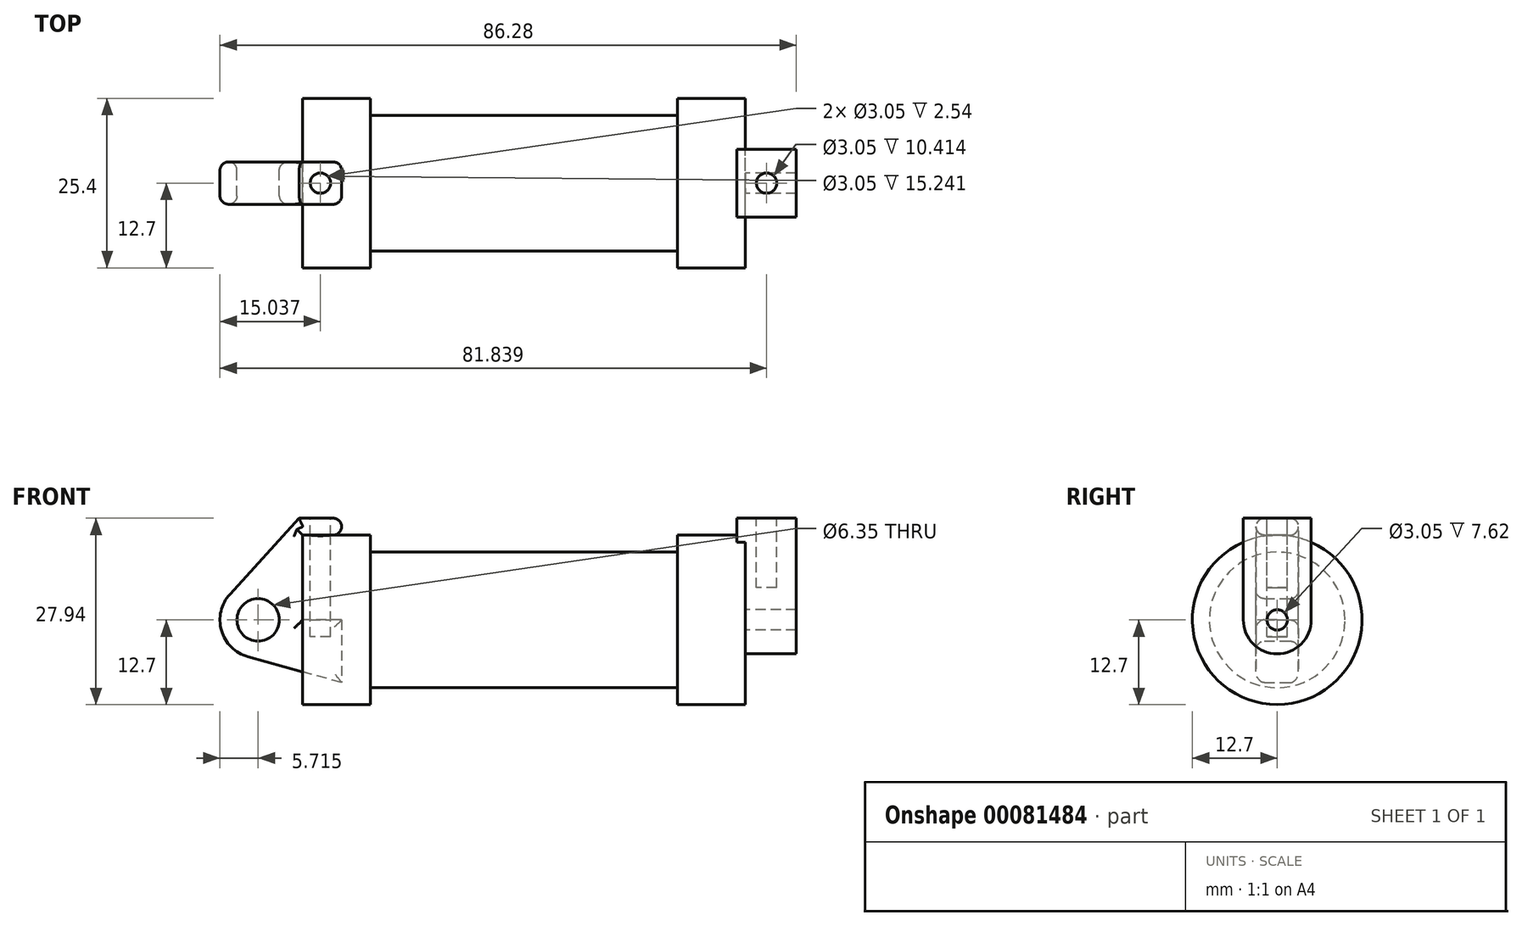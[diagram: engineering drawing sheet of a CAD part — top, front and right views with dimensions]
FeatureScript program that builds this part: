
annotation { "Feature Type Name" : "Feature", "Feature Type Description" : "" }
export const myFeature = defineFeature(function(context is Context, id is Id, definition is map)
    precondition{}
    {
        {
            var Q0;
            Q0=qCreatedBy(makeId("Front.planeOp"),FACE);
            var sketch = newSketch(context, id + "F0", { "sketchPlane" : qUnion([Q0])});
            skLineSegment(sketch, "E0", {"start": v(0, 0) * mm, "end": v(0, 12.7) * mm});
            skLineSegment(sketch, "E1", {"start": v(0, 12.7) * mm, "end": v(10.16, 12.7) * mm});
            skLineSegment(sketch, "E2", {"start": v(10.16, 12.7) * mm, "end": v(10.16, 10.16) * mm});
            skLineSegment(sketch, "E3", {"start": v(10.16, 10.16) * mm, "end": v(56.13, 10.16) * mm});
            skLineSegment(sketch, "E4", {"start": v(56.13, 10.16) * mm, "end": v(56.13, 12.7) * mm});
            skLineSegment(sketch, "E5", {"start": v(56.13, 12.7) * mm, "end": v(66.3, 12.7) * mm});
            skLineSegment(sketch, "E6", {"start": v(66.3, 12.7) * mm, "end": v(66.3, 0) * mm});
            skLineSegment(sketch, "E7", {"start": v(66.3, 0) * mm, "end": v(0, 0) * mm});
            skLineSegment(sketch, "E8", {"start": v(5.84, 15.24) * mm, "end": v(-0.5, 15.24) * mm});
            skLineSegment(sketch, "E9", {"start": v(-0.5, 15.24) * mm, "end": v(-10.88, 3.85) * mm});
            skLineSegment(sketch, "E10", {"start": v(0, 0) * mm, "end": v(-6.65, 0) * mm});
            skCircle(sketch, "E11", {"center": v(-6.65, 0) * mm, "radius": 5.72 * mm});
            skCircle(sketch, "E12", {"center": v(-6.65, 0) * mm, "radius": 3.18 * mm});
            skLineSegment(sketch, "E13", {"start": v(5.84, 15.24) * mm, "end": v(5.84, -9.4) * mm});
            skLineSegment(sketch, "E14", {"start": v(5.84, -9.4) * mm, "end": v(-8.18, -5.5) * mm});
            skSolve(sketch);
        }
        {
            var Q0;
            {var subQ0=sQuery(id+"F0.wireOp",EDGE,"E2");Q0=makeQuery(id+"F0.imprint","IMPRINT",FACE,{"disambiguationData":[TD([[makeQuery(id+"F0.imprint","IMPRINT",EDGE,{"derivedFrom":subQ0}),-1.0]])]});}
            var Q1;
            {var subQ0=sQuery(id+"F0.wireOp",EDGE,"E0");Q1=makeQuery(id+"F0.imprint","IMPRINT",FACE,{"disambiguationData":[TD([[makeQuery(id+"F0.imprint","IMPRINT",EDGE,{"derivedFrom":subQ0}),-1.0]])]});}
            var Q2;
            Q2=sQuery(id+"F0.wireOp",EDGE,"E7");
            revolve(context, id + "F1", {"entities" : qUnion([Q0, Q1]), "axis" : qUnion([Q2]), "revolveType" : RevolveType.FULL});
        }
        {
            var Q0;
            {var subQ3=sQuery(id+"F0.wireOp",EDGE,"E0");Q0=makeQuery(id+"F0.imprint","IMPRINT",FACE,{"disambiguationData":[TD([[makeQuery(id+"F0.imprint","IMPRINT",EDGE,{"derivedFrom":subQ3}),1.0]])]});}
            var Q1;
            {var subQ4=sQuery(id+"F0.wireOp",EDGE,"E12");Q1=makeQuery(id+"F0.imprint","IMPRINT",FACE,{"disambiguationData":[TD([[makeQuery(id+"F0.imprint","IMPRINT",EDGE,{"derivedFrom":subQ4}),-1.0]])]});}
            var Q2;
            {var subQ0=sQuery(id+"F0.wireOp",EDGE,"E14");Q2=makeQuery(id+"F0.imprint","IMPRINT",FACE,{"disambiguationData":[TD([[makeQuery(id+"F0.imprint","IMPRINT",EDGE,{"derivedFrom":subQ0}),-1.0]])]});}
            extrude(context, id + "F2", {"entities" : qUnion([Q0, Q1, Q2]), "endBound" : BoundingType.SYMMETRIC, "depth" : 6.35 * mm});
        }
        {
            var Q0;
            Q0=makeQuery(id+"F1.opRevolve","SWEPT_FACE",FACE,{"disambiguationData":[OSD([sQuery(id+"F0.wireOp",EDGE,"E6")])]});
            var sketch = newSketch(context, id + "F3", { "sketchPlane" : qUnion([Q0])});
            skCircle(sketch, "E15", {"center": v(0, 0) * mm, "radius": 1.52 * mm});
            skCircle(sketch, "E16", {"center": v(0, 0) * mm, "radius": 5.08 * mm});
            skLineSegment(sketch, "E17", {"start": v(5.08, 0) * mm, "end": v(5.08, 15.24) * mm});
            skLineSegment(sketch, "E18", {"start": v(-5.08, 0) * mm, "end": v(-5.08, 15.24) * mm});
            skLineSegment(sketch, "E19", {"start": v(-5.08, 15.24) * mm, "end": v(5.08, 15.24) * mm});
            skSolve(sketch);
        }
        {
            var Q0;
            Q0=makeQuery(id+"F3.imprint","IMPRINT",FACE,{"disambiguationData":[TD([[makeQuery(id+"F3.imprint","IMPRINT",EDGE,{"derivedFrom":sQuery(id+"F3.wireOp",EDGE,"E15")}),-1.0]])]});
            var Q1;
            {var subQ0=sQuery(id+"F3.wireOp",EDGE,"E19");Q1=makeQuery(id+"F3.imprint","IMPRINT",FACE,{"disambiguationData":[TD([[makeQuery(id+"F3.imprint","IMPRINT",EDGE,{"derivedFrom":subQ0}),-1.0]])]});}
            var Q2;
            {var subQ0=sQuery(id+"F3.wireOp",EDGE,"E17");var subQ1=sQuery(id+"F3.wireOp",EDGE,"E16");var subQ2=makeQuery(id+"F3.imprint","INTERSECT",VERTEX,{"derivedFrom":[subQ1,subQ0]});Q2=makeQuery(id+"F3.imprint","IMPRINT",FACE,{"disambiguationData":[TD([[makeQuery(id+"F3.imprint","IMPRINT",EDGE,{"disambiguationData":[TD([[subQ2,-1.0]])],"derivedFrom":subQ1}),-1.0]])]});}
            extrude(context, id + "F4", {"entities" : qUnion([Q0, Q1, Q2]), "operationType" : NewBodyOperationType.ADD, "depth" : 7.62 * mm});
        }
        {
            var Q0;
            Q0=makeQuery(id+"F4.opExtrude","CAP_FACE",FACE,{"disambiguationData":[OSD([sQuery(id+"F3.wireOp",EDGE,"E15"),sQuery(id+"F3.wireOp",EDGE,"E16"),sQuery(id+"F3.wireOp",EDGE,"E17"),sQuery(id+"F3.wireOp",EDGE,"E18"),sQuery(id+"F3.wireOp",EDGE,"E19")])],"isStart":true});
            extrude(context, id + "F5", {"entities" : qUnion([Q0]), "operationType" : NewBodyOperationType.ADD, "depth" : 1.27 * mm});
        }
        {
            var Q0;
            Q0=makeQuery(id+"F4.boolean.opBoolean","SPLIT",FACE,{"disambiguationData":[TD([makeQuery(id+"F4.opExtrude","SWEPT_FACE",FACE,{"disambiguationData":[OSD([sQuery(id+"F3.wireOp",EDGE,"E15")])]})])],"derivedFrom":makeQuery(id+"F1.opRevolve","SWEPT_FACE",FACE,{"disambiguationData":[OSD([sQuery(id+"F0.wireOp",EDGE,"E6")])]})});
            extrude(context, id + "F6", {"entities" : qUnion([Q0]), "operationType" : NewBodyOperationType.ADD, "oppositeDirection" : true, "depth" : 1.27 * mm});
        }
        {
            var Q0;
            {var subQ0=sQuery(id+"F3.wireOp",EDGE,"E19");Q0=makeQuery(id+"F5.boolean.opBoolean","MERGE",FACE,{"derivedFrom":[makeQuery(id+"F4.opExtrude","SWEPT_FACE",FACE,{"disambiguationData":[OSD([subQ0])]}),makeQuery(id+"F5.opExtrude","SWEPT_FACE",FACE,{"disambiguationData":[OSD([subQ0])]})]});}
            var sketch = newSketch(context, id + "F7", { "sketchPlane" : qUnion([Q0])});
            skCircle(sketch, "E20", {"center": v(69.47, 0) * mm, "radius": 1.52 * mm});
            skSolve(sketch);
        }
        {
            var Q0;
            Q0=makeQuery(id+"F7.imprint","IMPRINT",FACE,{"disambiguationData":[TD([[makeQuery(id+"F7.imprint","IMPRINT",EDGE,{"derivedFrom":sQuery(id+"F7.wireOp",EDGE,"E20")}),1.0]])]});
            extrude(context, id + "F8", {"entities" : qUnion([Q0]), "operationType" : NewBodyOperationType.REMOVE, "oppositeDirection" : true, "depth" : 10.4 * mm});
        }
        {
            var Q0;
            Q0=makeQuery(id+"F1.opRevolve","SWEPT_EDGE",EDGE,{"disambiguationData":[OSD([sQuery(id+"F0.wireOp",EDGE,"E0"),sQuery(id+"F0.wireOp",EDGE,"E1")])]});
            var Q1;
            Q1=makeQuery(id+"F1.opRevolve","SWEPT_EDGE",EDGE,{"disambiguationData":[OSD([sQuery(id+"F0.wireOp",EDGE,"E1"),sQuery(id+"F0.wireOp",EDGE,"E2")])]});
            var Q2;
            Q2=makeQuery(id+"F1.opRevolve","SWEPT_EDGE",EDGE,{"disambiguationData":[OSD([sQuery(id+"F0.wireOp",EDGE,"E4"),sQuery(id+"F0.wireOp",EDGE,"E5")])]});
            var Q3;
            Q3=makeQuery(id+"F4.boolean.opBoolean","SPLIT",EDGE,{"disambiguationData":[OD(1.0)],"derivedFrom":makeQuery(id+"F1.opRevolve","SWEPT_EDGE",EDGE,{"disambiguationData":[OSD([sQuery(id+"F0.wireOp",EDGE,"E5"),sQuery(id+"F0.wireOp",EDGE,"E6")])]})});
            var Q4;
            Q4=makeQuery(id+"F4.opExtrude","CAP_EDGE",EDGE,{"disambiguationData":[OSD([sQuery(id+"F3.wireOp",EDGE,"E18")])],"isStart":false});
            var Q5;
            Q5=makeQuery(id+"F4.opExtrude","SWEPT_EDGE",EDGE,{"disambiguationData":[OSD([sQuery(id+"F3.wireOp",EDGE,"E16"),sQuery(id+"F3.wireOp",EDGE,"E18")])]});
            var Q6;
            {var subQ0=sQuery(id+"F3.wireOp",EDGE,"E16");var subQ1=sQuery(id+"F3.wireOp",EDGE,"E18");Q6=makeQuery(id+"F4.boolean.opBoolean","SPLIT",EDGE,{"disambiguationData":[TD([makeQuery(id+"F4.opExtrude","SWEPT_FACE",FACE,{"disambiguationData":[OSD([subQ0])]})])],"derivedFrom":makeQuery(id+"F4.opExtrude","CAP_EDGE",EDGE,{"disambiguationData":[OSD([subQ1])],"isStart":true})});}
            var Q7;
            Q7=makeQuery(id+"F5.opExtrude","CAP_EDGE",EDGE,{"disambiguationData":[OSD([sQuery(id+"F3.wireOp",EDGE,"E18")])],"isStart":false});
            var Q8;
            Q8=makeQuery(id+"F5.opExtrude","CAP_EDGE",EDGE,{"disambiguationData":[OSD([sQuery(id+"F3.wireOp",EDGE,"E19")])],"isStart":false});
            var Q9;
            {var subQ0=sQuery(id+"F3.wireOp",EDGE,"E19");var subQ1=sQuery(id+"F3.wireOp",EDGE,"E18");Q9=makeQuery(id+"F5.boolean.opBoolean","MERGE",EDGE,{"derivedFrom":[makeQuery(id+"F4.opExtrude","SWEPT_EDGE",EDGE,{"disambiguationData":[OSD([subQ1,subQ0])]}),makeQuery(id+"F5.opExtrude","SWEPT_EDGE",EDGE,{"disambiguationData":[OSD([subQ1,subQ0])]})]});}
            var Q10;
            Q10=makeQuery(id+"F4.opExtrude","CAP_EDGE",EDGE,{"disambiguationData":[OSD([sQuery(id+"F3.wireOp",EDGE,"E19")])],"isStart":false});
            var Q11;
            {var subQ0=sQuery(id+"F3.wireOp",EDGE,"E19");var subQ1=sQuery(id+"F3.wireOp",EDGE,"E17");Q11=makeQuery(id+"F5.boolean.opBoolean","MERGE",EDGE,{"derivedFrom":[makeQuery(id+"F4.opExtrude","SWEPT_EDGE",EDGE,{"disambiguationData":[OSD([subQ1,subQ0])]}),makeQuery(id+"F5.opExtrude","SWEPT_EDGE",EDGE,{"disambiguationData":[OSD([subQ1,subQ0])]})]});}
            var Q12;
            Q12=makeQuery(id+"F4.opExtrude","CAP_EDGE",EDGE,{"disambiguationData":[OSD([sQuery(id+"F3.wireOp",EDGE,"E16")])],"isStart":false});
            var Q13;
            Q13=makeQuery(id+"F4.opExtrude","CAP_EDGE",EDGE,{"disambiguationData":[OSD([sQuery(id+"F3.wireOp",EDGE,"E16")])],"isStart":true});
            var Q14;
            Q14=makeQuery(id+"F4.opExtrude","CAP_EDGE",EDGE,{"disambiguationData":[OSD([sQuery(id+"F3.wireOp",EDGE,"E17")])],"isStart":false});
            var Q15;
            {var subQ0=sQuery(id+"F3.wireOp",EDGE,"E16");var subQ1=sQuery(id+"F3.wireOp",EDGE,"E17");Q15=makeQuery(id+"F4.boolean.opBoolean","SPLIT",EDGE,{"disambiguationData":[TD([makeQuery(id+"F4.opExtrude","SWEPT_FACE",FACE,{"disambiguationData":[OSD([subQ0])]})])],"derivedFrom":makeQuery(id+"F4.opExtrude","CAP_EDGE",EDGE,{"disambiguationData":[OSD([subQ1])],"isStart":true})});}
            var Q16;
            Q16=makeQuery(id+"F5.opExtrude","CAP_EDGE",EDGE,{"disambiguationData":[OSD([sQuery(id+"F3.wireOp",EDGE,"E17")])],"isStart":false});
            var Q17;
            Q17=makeQuery(id+"F1.opRevolve","SWEPT_EDGE",EDGE,{"disambiguationData":[OSD([sQuery(id+"F0.wireOp",EDGE,"E2"),sQuery(id+"F0.wireOp",EDGE,"E3")])]});
            var Q18;
            Q18=makeQuery(id+"F1.opRevolve","SWEPT_EDGE",EDGE,{"disambiguationData":[OSD([sQuery(id+"F0.wireOp",EDGE,"E3"),sQuery(id+"F0.wireOp",EDGE,"E4")])]});
            var Q19;
            {var subQ0=sQuery(id+"F3.wireOp",EDGE,"E17");var subQ1=sQuery(id+"F3.wireOp",EDGE,"E19");var subQ2=sQuery(id+"F3.wireOp",EDGE,"E18");var subQ3=sQuery(id+"F3.wireOp",EDGE,"E16");var subQ4=sQuery(id+"F3.wireOp",EDGE,"E15");var subQ5=sQuery(id+"F0.wireOp",EDGE,"E6");var subQ6=sQuery(id+"F0.wireOp",EDGE,"E5");Q19=makeQuery(id+"F5.opExtrude","SWEPT_EDGE",EDGE,{"disambiguationData":[OSD([subQ6,subQ5,subQ4,subQ3,subQ0,subQ2,subQ1]),TDD([makeQuery(id+"F4.boolean.opBoolean","TWEAK_VERTEX",VERTEX,{"derivedFrom":[makeQuery(id+"F1.opRevolve","SWEPT_FACE",FACE,{"disambiguationData":[OSD([subQ6])]}),makeQuery(id+"F1.opRevolve","SWEPT_FACE",FACE,{"disambiguationData":[OSD([subQ5])]}),makeQuery(id+"F4.opExtrude","CAP_FACE",FACE,{"disambiguationData":[OSD([subQ4,subQ3,subQ0,subQ2,subQ1])],"isStart":true}),makeQuery(id+"F4.opExtrude","SWEPT_FACE",FACE,{"disambiguationData":[OSD([subQ0])]})]})])]});}
            var Q20;
            {var subQ0=sQuery(id+"F0.wireOp",EDGE,"E13");Q20=makeQuery(id+"F2.opExtrude","CAP_EDGE",EDGE,{"disambiguationData":[OSD([subQ0]),TDD([makeQuery(id+"F0.imprint","IMPRINT",EDGE,{"disambiguationData":[TD([[makeQuery(id+"F0.imprint","INTERSECT",VERTEX,{"derivedFrom":[sQuery(id+"F0.wireOp",EDGE,"E8"),subQ0]}),-1.0]])],"derivedFrom":subQ0})])],"isStart":false});}
            var Q21;
            Q21=makeQuery(id+"F2.opExtrude","SWEPT_EDGE",EDGE,{"disambiguationData":[OSD([sQuery(id+"F0.wireOp",EDGE,"E8"),sQuery(id+"F0.wireOp",EDGE,"E13")])]});
            var Q22;
            Q22=makeQuery(id+"F2.opExtrude","SWEPT_EDGE",EDGE,{"disambiguationData":[OSD([sQuery(id+"F0.wireOp",EDGE,"E1"),sQuery(id+"F0.wireOp",EDGE,"E13")])]});
            var Q23;
            {var subQ0=sQuery(id+"F0.wireOp",EDGE,"E13");Q23=makeQuery(id+"F2.opExtrude","CAP_EDGE",EDGE,{"disambiguationData":[OSD([subQ0]),TDD([makeQuery(id+"F0.imprint","IMPRINT",EDGE,{"disambiguationData":[TD([[makeQuery(id+"F0.imprint","INTERSECT",VERTEX,{"derivedFrom":[sQuery(id+"F0.wireOp",EDGE,"E8"),subQ0]}),-1.0]])],"derivedFrom":subQ0})])],"isStart":true});}
            var Q24;
            Q24=makeQuery(id+"F2.opExtrude","CAP_EDGE",EDGE,{"disambiguationData":[OSD([sQuery(id+"F0.wireOp",EDGE,"E1")])],"isStart":false});
            var Q25;
            Q25=makeQuery(id+"F2.opExtrude","CAP_EDGE",EDGE,{"disambiguationData":[OSD([sQuery(id+"F0.wireOp",EDGE,"E8")])],"isStart":false});
            var Q26;
            Q26=makeQuery(id+"F2.opExtrude","CAP_EDGE",EDGE,{"disambiguationData":[OSD([sQuery(id+"F0.wireOp",EDGE,"E9")])],"isStart":false});
            var Q27;
            Q27=makeQuery(id+"F2.opExtrude","CAP_EDGE",EDGE,{"disambiguationData":[OSD([sQuery(id+"F0.wireOp",EDGE,"E1")])],"isStart":true});
            var Q28;
            Q28=makeQuery(id+"F2.opExtrude","CAP_EDGE",EDGE,{"disambiguationData":[OSD([sQuery(id+"F0.wireOp",EDGE,"E8")])],"isStart":true});
            var Q29;
            Q29=makeQuery(id+"F2.opExtrude","CAP_EDGE",EDGE,{"disambiguationData":[OSD([sQuery(id+"F0.wireOp",EDGE,"E9")])],"isStart":true});
            var Q30;
            Q30=makeQuery(id+"F2.opExtrude","CAP_EDGE",EDGE,{"disambiguationData":[OSD([sQuery(id+"F0.wireOp",EDGE,"E11")])],"isStart":true});
            var Q31;
            Q31=makeQuery(id+"F2.opExtrude","CAP_EDGE",EDGE,{"disambiguationData":[OSD([sQuery(id+"F0.wireOp",EDGE,"E14")])],"isStart":true});
            var Q32;
            Q32=makeQuery(id+"F2.opExtrude","CAP_EDGE",EDGE,{"disambiguationData":[OSD([sQuery(id+"F0.wireOp",EDGE,"E0")])],"isStart":true});
            var Q33;
            Q33=makeQuery(id+"F2.opExtrude","CAP_EDGE",EDGE,{"disambiguationData":[OSD([sQuery(id+"F0.wireOp",EDGE,"E14")])],"isStart":false});
            var Q34;
            Q34=makeQuery(id+"F2.opExtrude","CAP_EDGE",EDGE,{"disambiguationData":[OSD([sQuery(id+"F0.wireOp",EDGE,"E11")])],"isStart":false});
            var Q35;
            Q35=makeQuery(id+"F2.opExtrude","SWEPT_EDGE",EDGE,{"disambiguationData":[OSD([sQuery(id+"F0.wireOp",EDGE,"E9"),sQuery(id+"F0.wireOp",EDGE,"E11")])]});
            var Q36;
            Q36=makeQuery(id+"F2.opExtrude","SWEPT_EDGE",EDGE,{"disambiguationData":[OSD([sQuery(id+"F0.wireOp",EDGE,"E11"),sQuery(id+"F0.wireOp",EDGE,"E14")])]});
            var Q37;
            Q37=makeQuery(id+"F2.opExtrude","CAP_EDGE",EDGE,{"disambiguationData":[OSD([sQuery(id+"F0.wireOp",EDGE,"E0")])],"isStart":false});
            var Q38;
            Q38=makeQuery(id+"F1.opRevolve","SWEPT_FACE",FACE,{"disambiguationData":[OSD([sQuery(id+"F0.wireOp",EDGE,"E1")])]});
            var Q39;
            Q39=makeQuery(id+"F2.opExtrude","CAP_FACE",FACE,{"disambiguationData":[OSD([sQuery(id+"F0.wireOp",EDGE,"E0"),sQuery(id+"F0.wireOp",EDGE,"E1"),sQuery(id+"F0.wireOp",EDGE,"E7"),sQuery(id+"F0.wireOp",EDGE,"E8"),sQuery(id+"F0.wireOp",EDGE,"E9"),sQuery(id+"F0.wireOp",EDGE,"E11"),sQuery(id+"F0.wireOp",EDGE,"E12"),sQuery(id+"F0.wireOp",EDGE,"E13"),sQuery(id+"F0.wireOp",EDGE,"E14")])],"isStart":false});
            var Q40;
            {var subQ0=sQuery(id+"F0.wireOp",EDGE,"E13");Q40=makeQuery(id+"F2.opExtrude","SWEPT_FACE",FACE,{"disambiguationData":[OSD([subQ0]),TDD([makeQuery(id+"F0.imprint","IMPRINT",EDGE,{"disambiguationData":[TD([[makeQuery(id+"F0.imprint","INTERSECT",VERTEX,{"derivedFrom":[sQuery(id+"F0.wireOp",EDGE,"E8"),subQ0]}),-1.0]])],"derivedFrom":subQ0})])]});}
            var Q41;
            Q41=makeQuery(id+"F2.opExtrude","CAP_FACE",FACE,{"disambiguationData":[OSD([sQuery(id+"F0.wireOp",EDGE,"E0"),sQuery(id+"F0.wireOp",EDGE,"E1"),sQuery(id+"F0.wireOp",EDGE,"E7"),sQuery(id+"F0.wireOp",EDGE,"E8"),sQuery(id+"F0.wireOp",EDGE,"E9"),sQuery(id+"F0.wireOp",EDGE,"E11"),sQuery(id+"F0.wireOp",EDGE,"E12"),sQuery(id+"F0.wireOp",EDGE,"E13"),sQuery(id+"F0.wireOp",EDGE,"E14")])],"isStart":true});
            fillet(context, id + "F9", {"entities" : qUnion([Q0, Q1, Q2, Q3, Q4, Q5, Q6, Q7, Q8, Q9, Q10, Q11, Q12, Q13, Q14, Q15, Q16, Q17, Q18, Q19, Q20, Q21, Q22, Q23, Q24, Q25, Q26, Q27, Q28, Q29, Q30, Q31, Q32, Q33, Q34, Q35, Q36, Q37, Q38, Q39, Q40, Q41]), "radius" : 1.27 * mm, "tangentPropagation" : true, "allowEdgeOverflow" : false});
        }
        {
            var Q0;
            Q0=makeQuery(id+"F2.opExtrude","SWEPT_FACE",FACE,{"disambiguationData":[OSD([sQuery(id+"F0.wireOp",EDGE,"E8")])]});
            var sketch = newSketch(context, id + "F10", { "sketchPlane" : qUnion([Q0])});
            skCircle(sketch, "E21", {"center": v(2.67, 0) * mm, "radius": 1.52 * mm});
            skSolve(sketch);
        }
        {
            var Q0;
            Q0=makeQuery(id+"F10.imprint","IMPRINT",FACE,{"disambiguationData":[TD([[makeQuery(id+"F10.imprint","IMPRINT",EDGE,{"derivedFrom":sQuery(id+"F10.wireOp",EDGE,"E21")}),1.0]])]});
            extrude(context, id + "F11", {"entities" : qUnion([Q0]), "operationType" : NewBodyOperationType.REMOVE, "oppositeDirection" : true, "depth" : 17.78 * mm});
        }
    });
